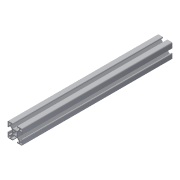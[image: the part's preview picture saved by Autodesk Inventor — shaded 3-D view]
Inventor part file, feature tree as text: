
AUTODESK INVENTOR PART (.ipt)
format: ipt  version: 2013 (Build 170138000, 138)  size: 275,968 bytes
history: native  units: in
note: dims shown in document units (in); Inventor stores cm internally (conversion verified against a paired STEP export)
features: other x3, extrude x1, sketch x1
ambient origin geometry x8: Origin, YZ Plane, XZ Plane, XY Plane, X Axis, Y Axis, Z Axis, Center Point
bodies: Solid1 (feature_tree)
feature tree (5):
  other  "Blocks"
  extrude  "Extrusion1"  [1 undecoded]
  sketch  "Sketch1"  dims[d1=0.0in]
  other  "Bosch 30x30 profile"
  other  "Bosch 30x30 profile:1"
note: 1 required parameter value undecoded (feature->parameter linkage not recoverable at this tier; creation-order binding heuristic only, values carry confidence <= 0.55)
